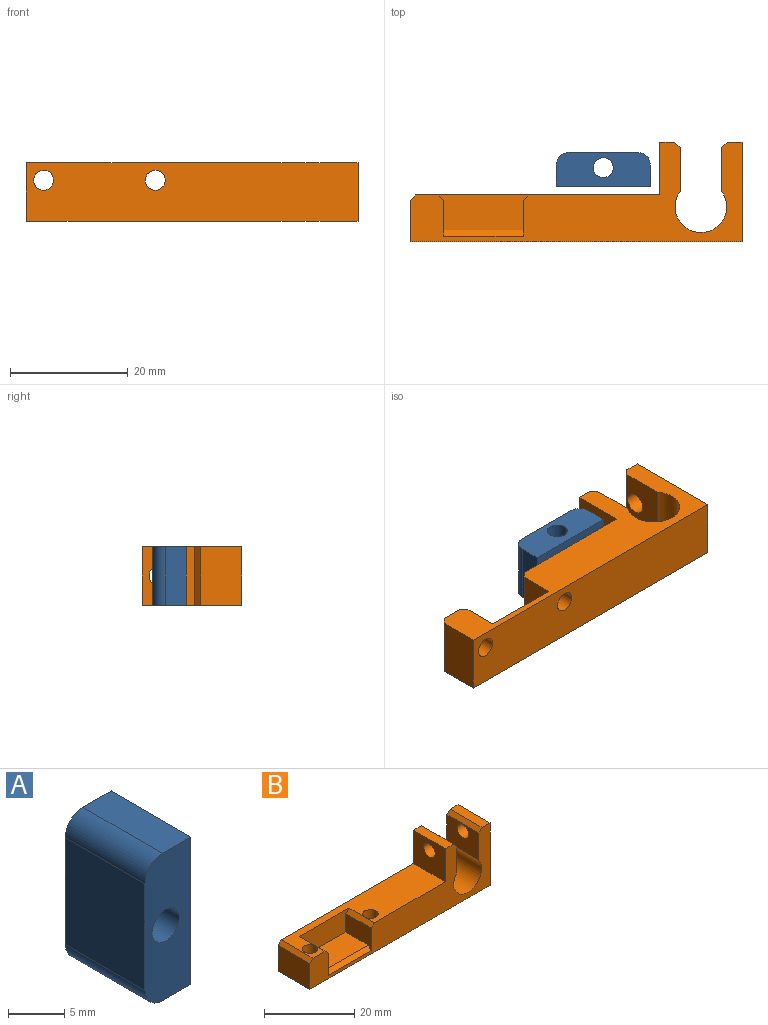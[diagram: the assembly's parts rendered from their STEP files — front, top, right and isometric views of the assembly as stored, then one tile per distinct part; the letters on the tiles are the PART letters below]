
ASSEMBLY  parts=2 mates=1
PART A: 9 faces, bbox 5.8x10x16 mm
  f0: plane 16x10mm, normal (1,0,0), area 160mm2, adj f1,f3,f5,f6
  f1: plane 10x3.55mm, normal (0,0,1), area 35.5mm2, adj f0,f5,f6,f7
  f2: plane 11.6x10mm, normal (-1,0,0), area 116mm2, adj f5,f6,f7,f8
  f3: plane 10x3.55mm, normal (0,0,-1), area 35.5mm2, adj f0,f5,f6,f8
  f4: cylinder r=1.7mm len=10mm, axis (0,1,0), area 106.8mm2, adj f5,f6
  f5: plane 16x5.75mm, normal (0,-1,0), area 80.8mm2, adj f0,f1,f2,f3,f4,f7,f8
  f6: plane 16x5.75mm, normal (0,1,0), area 80.8mm2, adj f0,f1,f2,f3,f4,f7,f8
  f7: cylinder r=2.2mm len=10mm, axis (0,1,0), area 34.6mm2, adj f1,f2,f5,f6
  f8: cylinder r=2.2mm len=10mm, axis (0,-1,0), area 34.6mm2, adj f2,f3,f5,f6
PART B: 26 faces, bbox 56.5x10x17 mm
  f0: plane 10x2.5mm, normal (0,0,1), area 25mm2, adj f1,f2,f3,f20
  f1: plane 56.5x17mm, normal (0,-1,0), area 370.3mm2, adj f0,f3,f4,f5,f6,f7,f8,f10
  f2: plane 56.5x17mm, normal (0,1,0), area 465.8mm2, adj f0,f3,f4,f5,f6,f7,f13,f15
  f3: plane 10x9mm, normal (-1,0,0), area 79.8mm2, adj f0,f1,f2,f13,f18
  f4: plane 17x10mm, normal (1,0,0), area 159.8mm2, adj f1,f2,f5,f6,f19
  f5: plane 10x2.5mm, normal (0,0,1), area 25mm2, adj f1,f2,f4,f21
  f6: plane 56.5x10mm, normal (0,0,-1), area 546.8mm2, adj f1,f2,f4,f7,f11,f12
  f7: plane 10x7mm, normal (-1,0,0), area 70mm2, adj f1,f2,f6,f23
  f8: plane 8x6mm, normal (1,0,0), area 40.5mm2, adj f1,f9,f14,f22,f24
  f9: plane 15.5x6mm, normal (0,-1,0), area 82mm2, adj f8,f10,f13,f14,f24,f25
  f10: plane 8x6mm, normal (-1,0,0), area 40.5mm2, adj f1,f9,f14,f22,f25
  f11: cylinder r=1.7mm len=8mm, axis (0,0,-1), area 85.5mm2, adj f6,f13
  f12: cylinder r=1.7mm len=8mm, axis (0,0,-1), area 85.5mm2, adj f6,f13
  f13: plane 41.5x10mm, normal (0,0,1), area 272.8mm2, adj f1,f2,f3,f9,f11,f12,f23,f24
  f14: plane 13.5x7mm, normal (0,0,1), area 94.5mm2, adj f8,f9,f10,f22
  f15: cylinder r=4.4mm len=10mm, axis (0,1,0), area 195.5mm2, adj f1,f2,f16,f17
  f16: plane 10x7.33mm, normal (-1,0,0), area 63.2mm2, adj f1,f2,f15,f19,f21
  f17: plane 10x7.33mm, normal (1,0,0), area 63.2mm2, adj f1,f2,f15,f18,f20
  f18: cylinder r=1.8mm len=3.6mm, axis (1,0,0), area 39.6mm2, adj f3,f17
  f19: cylinder r=1.8mm len=3.6mm, axis (1,0,0), area 39.6mm2, adj f4,f16
  f20: plane 10x1mm, normal (0.71,0,0.71), area 14.1mm2, adj f0,f1,f2,f17
  f21: plane 10x1mm, normal (-0.71,0,0.71), area 14.1mm2, adj f1,f2,f5,f16
  f22: plane 13.5x1mm, normal (0,-0.71,0.71), area 19.1mm2, adj f1,f8,f10,f14
  f23: plane 10x1mm, normal (-0.71,0,0.71), area 14.1mm2, adj f1,f2,f7,f13
  f24: plane 8x1mm, normal (0.71,0,0.71), area 11.3mm2, adj f1,f8,f9,f13
  f25: plane 8x1mm, normal (-0.71,0,0.71), area 11.3mm2, adj f1,f9,f10,f13
PLACE A rot(axis=(-0.58,0.58,-0.58),120deg) t=(-9.22,-5.8,7.09)mm
PLACE B rot(axis=(-1,0,0),90deg) t=(-1.94,-5.12,17.09)mm
MATE planar B.f2 <-> A.f4  axis (0,0,-1) through (-8.18,-0.12,5.04)mm
